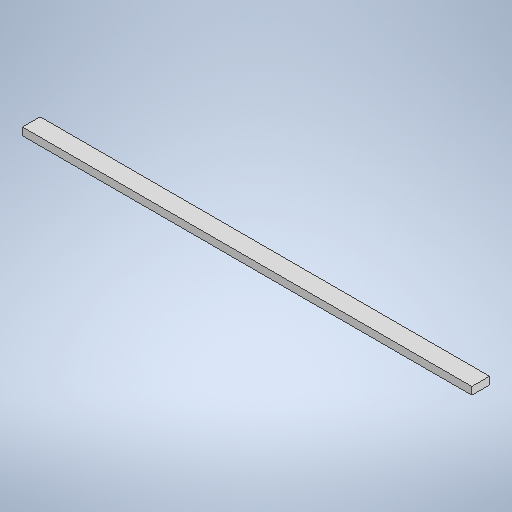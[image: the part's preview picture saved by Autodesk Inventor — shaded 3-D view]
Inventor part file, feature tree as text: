
AUTODESK INVENTOR PART (.ipt)
format: ipt  version: 2025 (Build 290162000, 162)  size: 247,808 bytes
history: native  units: in
note: dims shown in document units (in); Inventor stores cm internally (conversion verified against a paired STEP export)
features: extrude x1, sketch x1
ambient origin geometry x8: Origin, YZ Plane, XZ Plane, XY Plane, X Axis, Y Axis, Z Axis, Center Point
bodies: Solid1 (feature_tree)
feature tree (2):
  extrude  "Extrusion1"  Depth=3.5in
  sketch  "Sketch1"  dims[d0=89.0in d1=3.5in d2=1.5in d3=0.0in]
